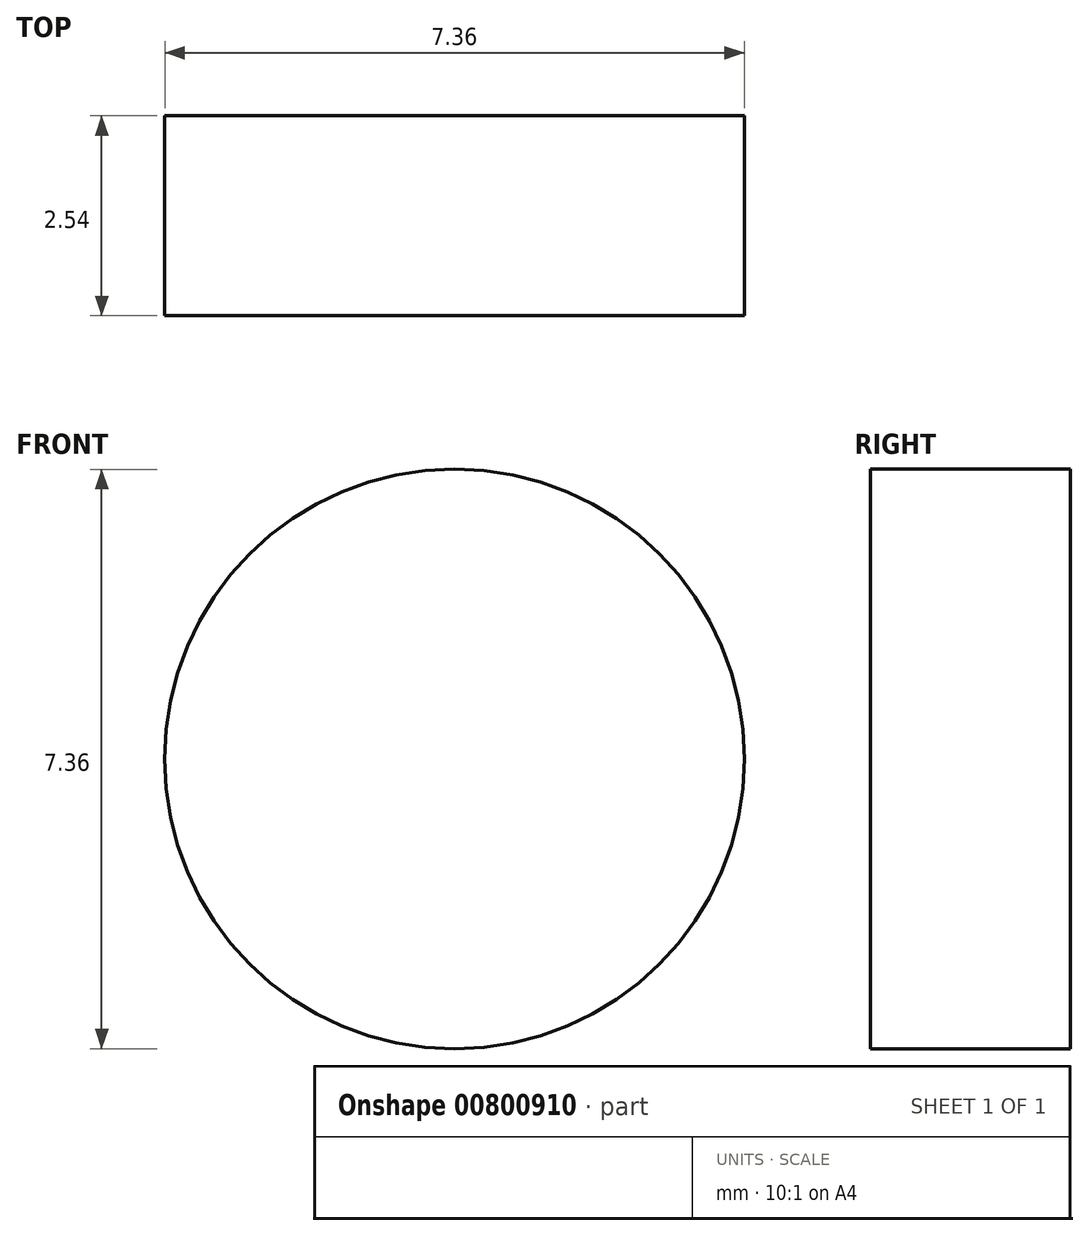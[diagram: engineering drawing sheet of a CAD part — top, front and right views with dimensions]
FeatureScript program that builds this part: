
annotation { "Feature Type Name" : "Feature", "Feature Type Description" : "" }
export const myFeature = defineFeature(function(context is Context, id is Id, definition is map)
    precondition{}
    {
        {
            var Q0;
            Q0=qCreatedBy(makeId("Front.planeOp"),FACE);
            var sketch = newSketch(context, id + "F0", { "sketchPlane" : qUnion([Q0])});
            skCircle(sketch, "E0", {"center": v(0, 0) * mm, "radius": 3.68 * mm});
            skSolve(sketch);
        }
        {
            var Q0;
            Q0 = qSketchRegion(id + "F0", true);
            extrude(context, id + "F1", {"entities" : qUnion([Q0]), "depth" : 2.54 * mm, "offsetDistance" : 25.4 * mm});
        }
    });
